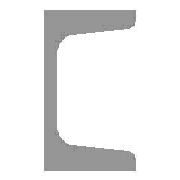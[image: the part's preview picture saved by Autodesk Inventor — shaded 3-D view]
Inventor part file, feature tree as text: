
AUTODESK INVENTOR PART (.ipt)
format: ipt  version: 2025 (Build 290162010, 162A)  size: 140,288 bytes
history: native  units: mm (DEFAULTED — no unit token found)
features: other x4, sketch x1, plane x1
ambient origin geometry x8: Origin, YZ Plane, XZ Plane, XY Plane, X Axis, Y Axis, Z Axis, Center Point
bodies: Solid1 (feature_tree), Body (feature_tree)
feature tree (6):
  parser-record x1  (decoder bookkeeping rows leaked as tree rows — omitted from the tree; the rows remain in map.json)
  other  "Driven Length"
  other  "Start Plane"
  other  "End Plane"
  sketch  "Sketch3"  dims[d0=5.9mm d1=50.0mm d2=50.0mm d3=8.0mm d4=22.05mm d5=2.317543mm d6=6500.0mm d7=0.0mm d23=8.0mm d24=4.5mm d25=1.51mm d26=-0.0mm d27=6500.0mm d28=90.0deg d29=6500.0mm]
  plane  "Work Plane3"
